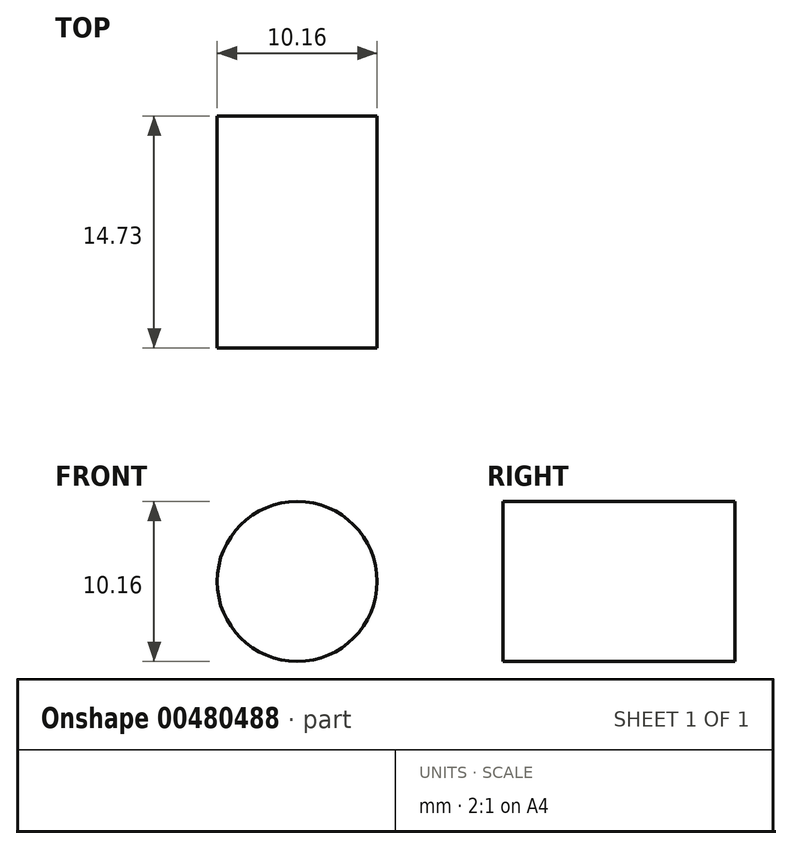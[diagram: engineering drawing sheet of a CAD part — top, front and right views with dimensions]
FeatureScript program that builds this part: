
annotation { "Feature Type Name" : "Feature", "Feature Type Description" : "" }
export const myFeature = defineFeature(function(context is Context, id is Id, definition is map)
    precondition{}
    {
        {
            var Q0;
            Q0=qCreatedBy(makeId("Front.planeOp"),FACE);
            var sketch = newSketch(context, id + "F0", { "sketchPlane" : qUnion([Q0])});
            skCircle(sketch, "E0", {"center": v(0, 0) * mm, "radius": 5.08 * mm});
            skSolve(sketch);
        }
        {
            var Q0;
            Q0 = qSketchRegion(id + "F0", true);
            extrude(context, id + "F1", {"entities" : qUnion([Q0]), "depth" : 14.73 * mm});
        }
    });
